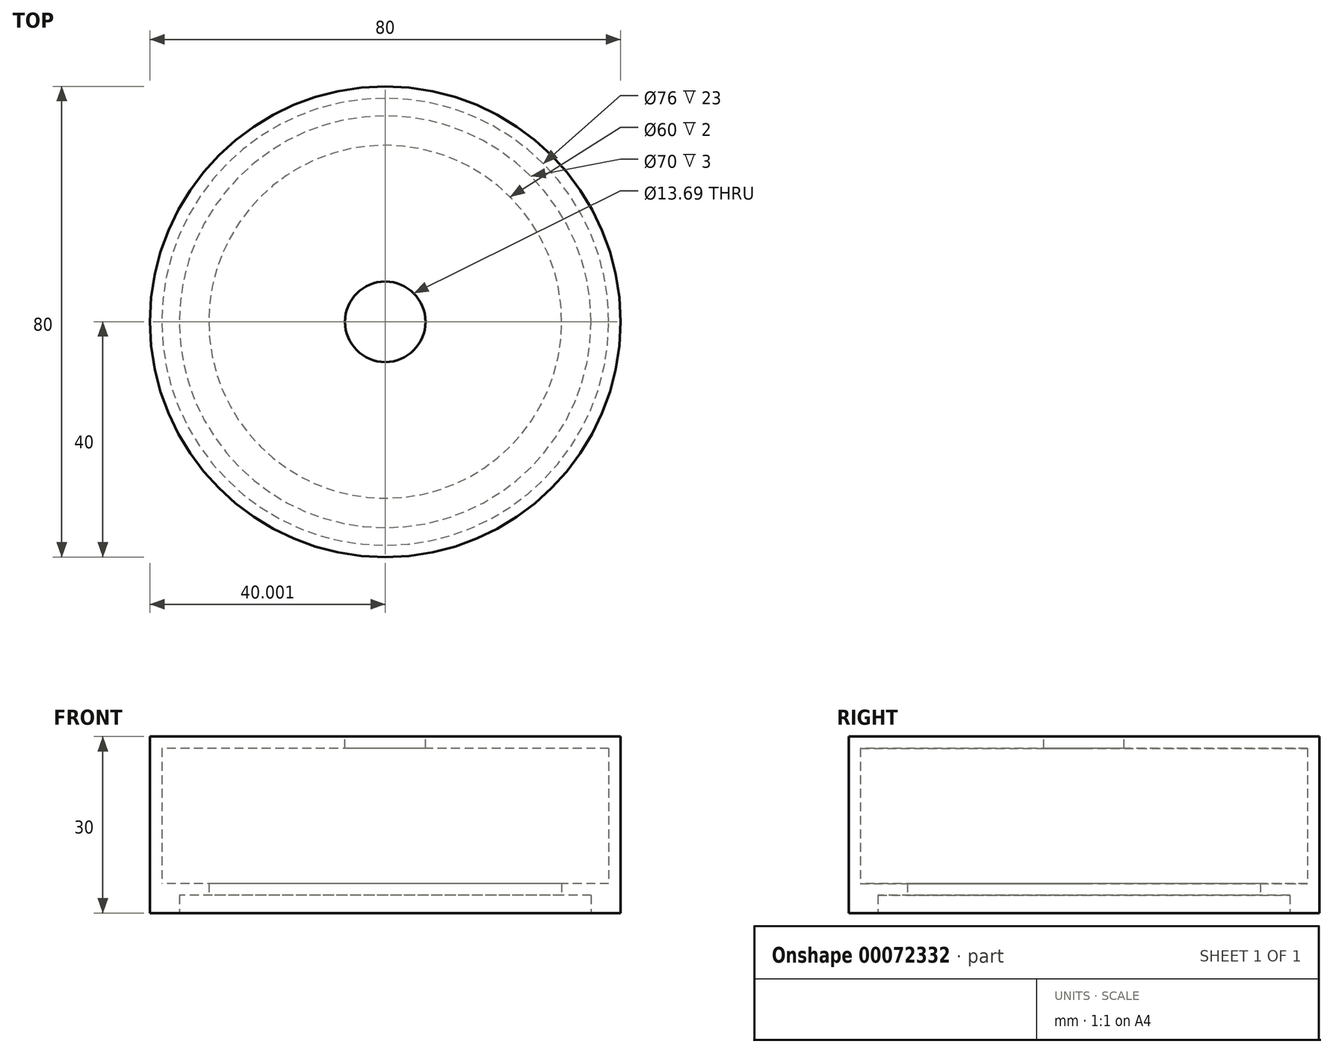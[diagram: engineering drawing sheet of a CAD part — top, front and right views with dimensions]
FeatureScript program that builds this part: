
annotation { "Feature Type Name" : "Feature", "Feature Type Description" : "" }
export const myFeature = defineFeature(function(context is Context, id is Id, definition is map)
    precondition{}
    {
        {
            var Q0;
            Q0=qCreatedBy(makeId("Top.planeOp"),FACE);
            var sketch = newSketch(context, id + "F0", { "sketchPlane" : qUnion([Q0])});
            skCircle(sketch, "E0", {"center": v(-34.64, 27.72) * mm, "radius": 40 * mm});
            skCircle(sketch, "E1", {"center": v(-34.64, 27.72) * mm, "radius": 38 * mm});
            skCircle(sketch, "E2", {"center": v(-34.64, 27.72) * mm, "radius": 35 * mm});
            skCircle(sketch, "E3", {"center": v(-34.64, 27.72) * mm, "radius": 30 * mm});
            skSolve(sketch);
        }
        {
            var Q0;
            Q0=makeQuery(id+"F0.imprint","IMPRINT",FACE,{"disambiguationData":[TD([[makeQuery(id+"F0.imprint","IMPRINT",EDGE,{"derivedFrom":sQuery(id+"F0.wireOp",EDGE,"E0")}),1.0]])]});
            extrude(context, id + "F1", {"entities" : qUnion([Q0]), "depth" : 30 * mm});
        }
        {
            var Q0;
            Q0=makeQuery(id+"F0.imprint","IMPRINT",FACE,{"disambiguationData":[TD([[makeQuery(id+"F0.imprint","IMPRINT",EDGE,{"derivedFrom":sQuery(id+"F0.wireOp",EDGE,"E1")}),1.0]])]});
            var Q1;
            Q1=makeQuery(id+"F0.imprint","IMPRINT",FACE,{"disambiguationData":[TD([[makeQuery(id+"F0.imprint","IMPRINT",EDGE,{"derivedFrom":sQuery(id+"F0.wireOp",EDGE,"E2")}),1.0]])]});
            extrude(context, id + "F2", {"entities" : qUnion([Q0, Q1]), "operationType" : NewBodyOperationType.ADD, "depth" : 5 * mm});
        }
        {
            var Q0;
            Q0=makeQuery(id+"F0.imprint","IMPRINT",FACE,{"disambiguationData":[TD([[makeQuery(id+"F0.imprint","IMPRINT",EDGE,{"derivedFrom":sQuery(id+"F0.wireOp",EDGE,"E2")}),1.0]])]});
            extrude(context, id + "F3", {"entities" : qUnion([Q0]), "operationType" : NewBodyOperationType.REMOVE, "depth" : 3 * mm});
        }
        {
            var Q0;
            Q0=makeQuery(id+"F1.opExtrude","CAP_FACE",FACE,{"disambiguationData":[OSD([sQuery(id+"F0.wireOp",EDGE,"E0"),sQuery(id+"F0.wireOp",EDGE,"E1")])],"isStart":false});
            var sketch = newSketch(context, id + "F4", { "sketchPlane" : qUnion([Q0])});
            skCircle(sketch, "E4.0", {"center": v(-34.64, 27.72) * mm, "radius": 40 * mm});
            skCircle(sketch, "E5", {"center": v(-34.64, 27.72) * mm, "radius": 39.95 * mm});
            skCircle(sketch, "E6", {"center": v(-34.64, 27.72) * mm, "radius": 6.84 * mm});
            skSolve(sketch);
        }
        {
            var Q0;
            Q0=makeQuery(id+"F4.imprint","IMPRINT",FACE,{"disambiguationData":[TD([[makeQuery(id+"F4.imprint","IMPRINT",EDGE,{"derivedFrom":sQuery(id+"F4.wireOp",EDGE,"E5")}),1.0]])]});
            var Q1;
            Q1=makeQuery(id+"F4.imprint","IMPRINT",FACE,{"disambiguationData":[TD([[makeQuery(id+"F4.imprint","IMPRINT",EDGE,{"derivedFrom":makeQuery(id+"F1.opExtrude","CAP_EDGE",EDGE,{"disambiguationData":[OSD([sQuery(id+"F0.wireOp",EDGE,"E1")])],"isStart":false})}),1.0]])]});
            extrude(context, id + "F5", {"entities" : qUnion([Q0, Q1]), "operationType" : NewBodyOperationType.ADD, "oppositeDirection" : true, "depth" : 2 * mm});
        }
    });
